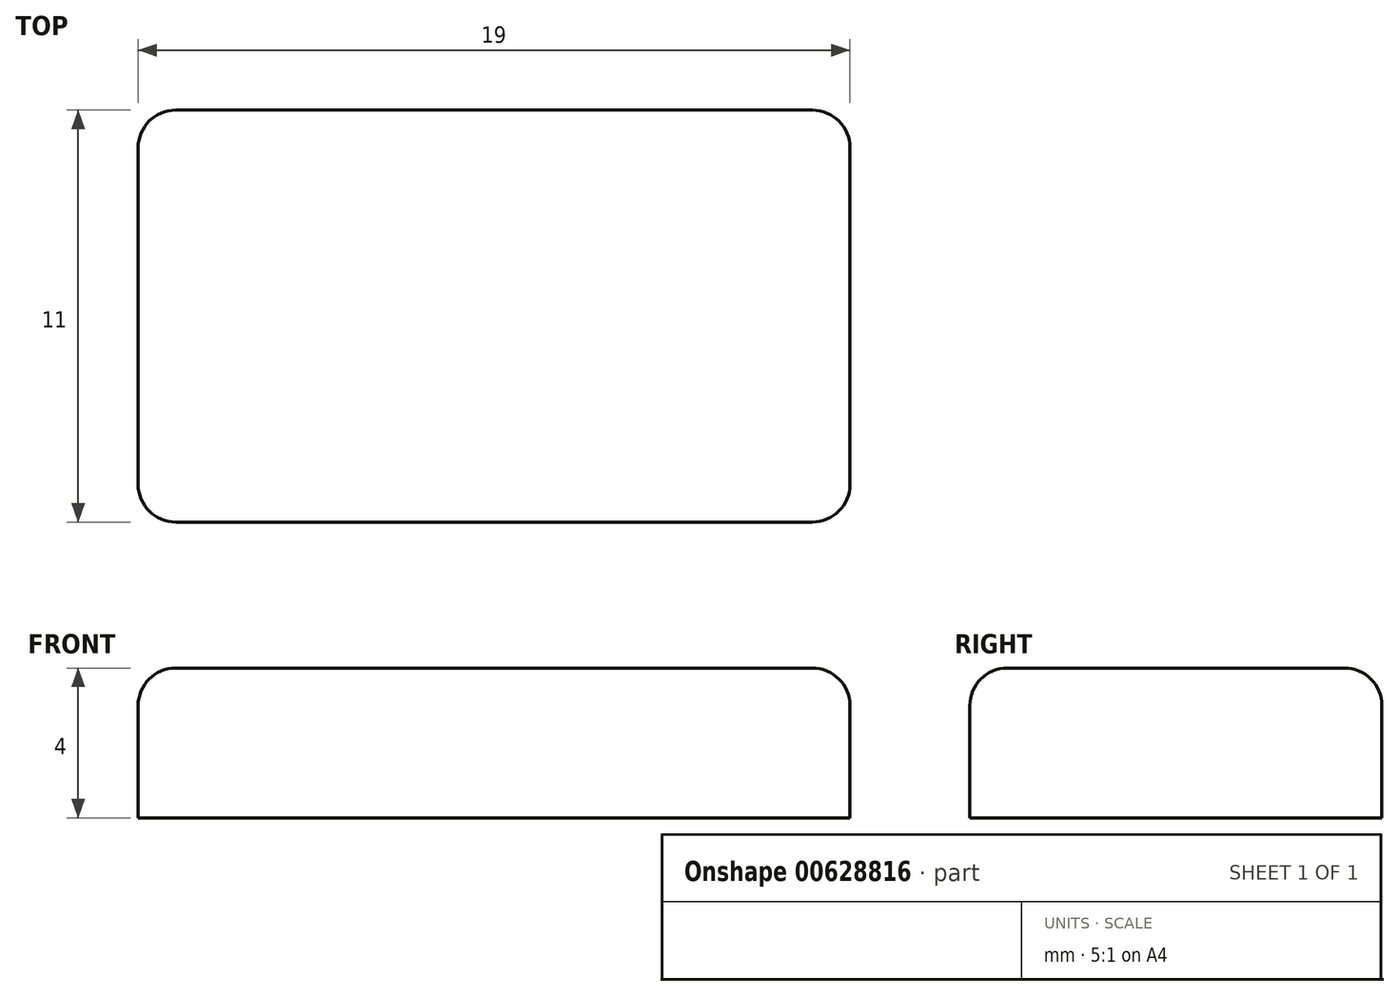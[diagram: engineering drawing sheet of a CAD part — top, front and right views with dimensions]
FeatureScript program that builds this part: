
annotation { "Feature Type Name" : "Feature", "Feature Type Description" : "" }
export const myFeature = defineFeature(function(context is Context, id is Id, definition is map)
    precondition{}
    {
        {
            var Q0;
            Q0=qCreatedBy(makeId("Top.planeOp"),FACE);
            var sketch = newSketch(context, id + "F0", { "sketchPlane" : qUnion([Q0])});
            skLineSegment(sketch, "E0.bottom", {"start": v(8.5, 5.5) * mm, "end": v(-8.5, 5.5) * mm});
            skLineSegment(sketch, "E0.top", {"start": v(8.5, -5.5) * mm, "end": v(-8.5, -5.5) * mm});
            skLineSegment(sketch, "E0.left", {"start": v(9.5, 4.5) * mm, "end": v(9.5, -4.5) * mm});
            skLineSegment(sketch, "E0.right", {"start": v(-9.5, 4.5) * mm, "end": v(-9.5, -4.5) * mm});
            skPoint(sketch, "E0.middle", {"position": v(0, 0) * mm});
            skPoint(sketch, "E1.visualSharp", {"position": v(-9.5, 5.5) * mm});
            skArc(sketch, "E1.filletArc", {"start": v(-8.5, 5.5) * mm, "mid": v(-9.2, 5.2) * mm, "end": v(-9.5, 4.5) * mm});
            skPoint(sketch, "E2.visualSharp", {"position": v(9.5, 5.5) * mm});
            skArc(sketch, "E2.filletArc", {"start": v(9.5, 4.5) * mm, "mid": v(9.2, 5.2) * mm, "end": v(8.5, 5.5) * mm});
            skPoint(sketch, "E3.visualSharp", {"position": v(9.5, -5.5) * mm});
            skArc(sketch, "E3.filletArc", {"start": v(8.5, -5.5) * mm, "mid": v(9.2, -5.2) * mm, "end": v(9.5, -4.5) * mm});
            skPoint(sketch, "E4.visualSharp", {"position": v(-9.5, -5.5) * mm});
            skArc(sketch, "E4.filletArc", {"start": v(-9.5, -4.5) * mm, "mid": v(-9.2, -5.2) * mm, "end": v(-8.5, -5.5) * mm});
            skSolve(sketch);
        }
        {
            var Q0;
            Q0 = qSketchRegion(id + "F0", true);
            extrude(context, id + "F1", {"entities" : qUnion([Q0]), "depth" : 4 * mm, "offsetDistance" : 25 * mm, "symmetric" : true});
        }
        {
            var Q0;
            Q0=makeQuery(id+"F1.opExtrude","CAP_EDGE",EDGE,{"disambiguationData":[OSD([sQuery(id+"F0.wireOp",EDGE,"E0.top")])],"isStart":false});
            fillet(context, id + "F2", {"entities" : qUnion([Q0]), "radius" : 1 * mm, "tangentPropagation" : true, "allowEdgeOverflow" : false});
        }
    });
